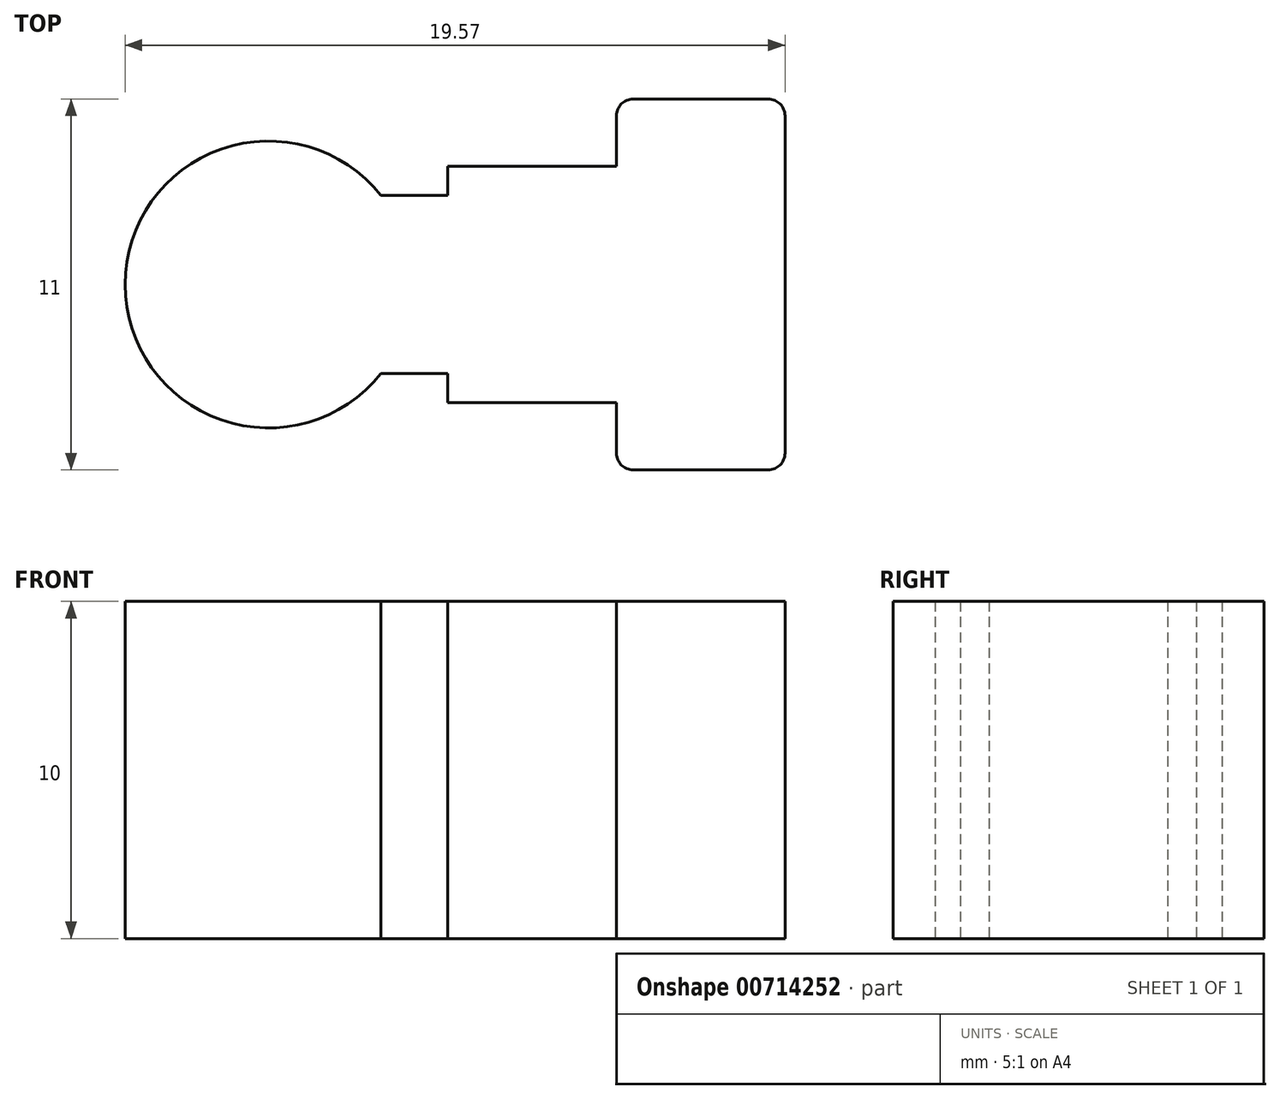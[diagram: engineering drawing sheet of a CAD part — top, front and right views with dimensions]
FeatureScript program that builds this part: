
annotation { "Feature Type Name" : "Feature", "Feature Type Description" : "" }
export const myFeature = defineFeature(function(context is Context, id is Id, definition is map)
    precondition{}
    {
        {
            var Q0;
            Q0=qCreatedBy(makeId("Top.planeOp"),FACE);
            var sketch = newSketch(context, id + "F0", { "sketchPlane" : qUnion([Q0])});
            skLineSegment(sketch, "E0", {"start": v(0, 0) * mm, "end": v(0, 5) * mm});
            skLineSegment(sketch, "E1", {"start": v(-0.5, 5.5) * mm, "end": v(-4.5, 5.5) * mm});
            skLineSegment(sketch, "E2", {"start": v(-5, 5) * mm, "end": v(-5, 3.5) * mm});
            skLineSegment(sketch, "E3", {"start": v(-5, 3.5) * mm, "end": v(-10, 3.5) * mm});
            skLineSegment(sketch, "E4", {"start": v(-10, 3.5) * mm, "end": v(-10, 0) * mm});
            skLineSegment(sketch, "E5.MirrorCS", {"start": v(-10, -3.5) * mm, "end": v(-10, 0) * mm});
            skLineSegment(sketch, "E6.MirrorCS", {"start": v(-5, -3.5) * mm, "end": v(-10, -3.5) * mm});
            skLineSegment(sketch, "E7.MirrorCS", {"start": v(-5, -5) * mm, "end": v(-5, -3.5) * mm});
            skLineSegment(sketch, "E8.MirrorCS", {"start": v(-0.5, -5.5) * mm, "end": v(-4.5, -5.5) * mm});
            skLineSegment(sketch, "E9.MirrorCS", {"start": v(0, 0) * mm, "end": v(0, -5) * mm});
            skPoint(sketch, "E10.visualSharp", {"position": v(0, -5.5) * mm});
            skArc(sketch, "E10.filletArc", {"start": v(-0.5, -5.5) * mm, "mid": v(-0.15, -5.35) * mm, "end": v(0, -5) * mm});
            skPoint(sketch, "E11.visualSharp", {"position": v(0, 5.5) * mm});
            skArc(sketch, "E11.filletArc", {"start": v(0, 5) * mm, "mid": v(-0.15, 5.35) * mm, "end": v(-0.5, 5.5) * mm});
            skPoint(sketch, "E12.visualSharp", {"position": v(-5, 5.5) * mm});
            skArc(sketch, "E12.filletArc", {"start": v(-4.5, 5.5) * mm, "mid": v(-4.85, 5.35) * mm, "end": v(-5, 5) * mm});
            skPoint(sketch, "E13.visualSharp", {"position": v(-5, -5.5) * mm});
            skArc(sketch, "E13.filletArc", {"start": v(-5, -5) * mm, "mid": v(-4.85, -5.35) * mm, "end": v(-4.5, -5.5) * mm});
            skSolve(sketch);
        }
        {
            var Q0;
            Q0=makeQuery(id+"F0.imprint","IMPRINT",FACE,{"disambiguationData":[TD([[makeQuery(id+"F0.imprint","IMPRINT",EDGE,{"derivedFrom":sQuery(id+"F0.wireOp",EDGE,"E0")}),1.0]])]});
            extrude(context, id + "F1", {"entities" : qUnion([Q0]), "depth" : 10 * mm, "offsetDistance" : 25 * mm});
        }
        {
            var Q0;
            Q0=qCreatedBy(makeId("Top.planeOp"),FACE);
            var sketch = newSketch(context, id + "F2", { "sketchPlane" : qUnion([Q0])});
            skCircle(sketch, "E14", {"center": v(-15.32, 0) * mm, "radius": 4.25 * mm});
            skLineSegment(sketch, "E15.bottom", {"start": v(-8.55, -2.64) * mm, "end": v(-12.6, -2.64) * mm});
            skLineSegment(sketch, "E15.top", {"start": v(-8.55, 2.64) * mm, "end": v(-12.6, 2.64) * mm});
            skLineSegment(sketch, "E15.left", {"start": v(-8.55, -2.64) * mm, "end": v(-8.55, 2.64) * mm});
            skLineSegment(sketch, "E15.right", {"start": v(-12.6, -2.64) * mm, "end": v(-12.6, 2.64) * mm});
            skPoint(sketch, "E15.middle", {"position": v(-10.57, 0) * mm});
            skSolve(sketch);
        }
        {
            var Q0;
            {var subQ5=sQuery(id+"F2.wireOp",EDGE,"E15.right");Q0=makeQuery(id+"F2.imprint","IMPRINT",FACE,{"disambiguationData":[TD([[makeQuery(id+"F2.imprint","IMPRINT",EDGE,{"derivedFrom":subQ5}),1.0]])]});}
            var Q1;
            {var subQ5=sQuery(id+"F2.wireOp",EDGE,"E15.right");Q1=makeQuery(id+"F2.imprint","IMPRINT",FACE,{"disambiguationData":[TD([[makeQuery(id+"F2.imprint","IMPRINT",EDGE,{"derivedFrom":subQ5}),-1.0]])]});}
            var Q2;
            {var subQ5=sQuery(id+"F2.wireOp",EDGE,"E15.left");Q2=makeQuery(id+"F2.imprint","IMPRINT",FACE,{"disambiguationData":[TD([[makeQuery(id+"F2.imprint","IMPRINT",EDGE,{"derivedFrom":subQ5}),1.0]])]});}
            extrude(context, id + "F3", {"entities" : qUnion([Q0, Q1, Q2]), "operationType" : NewBodyOperationType.ADD, "depth" : 10 * mm, "offsetDistance" : 25 * mm});
        }
    });
